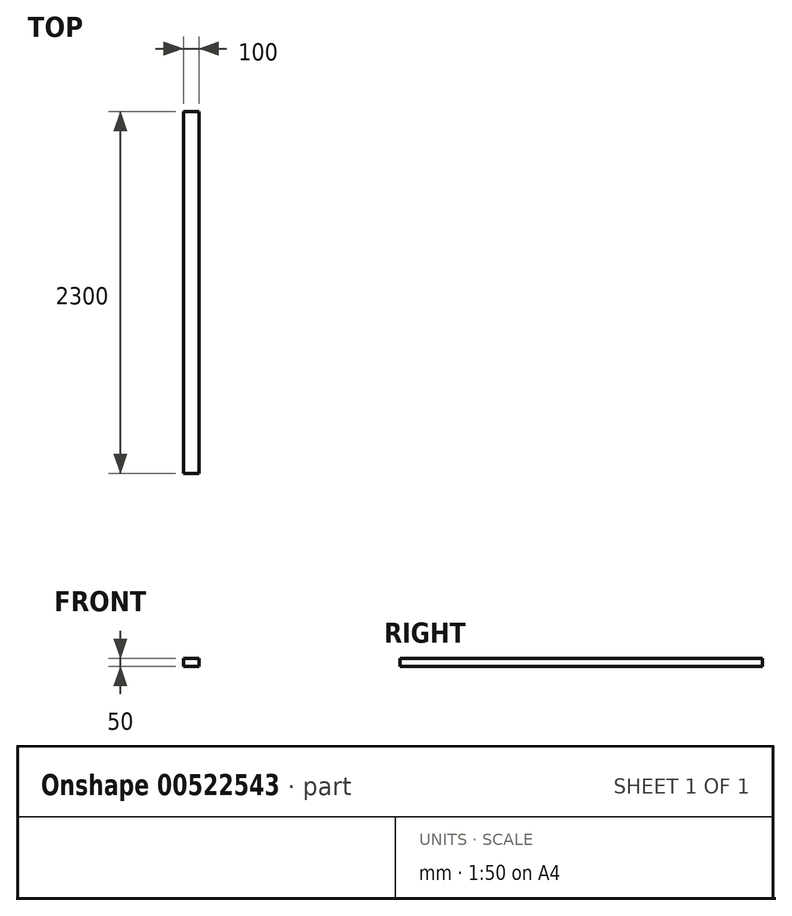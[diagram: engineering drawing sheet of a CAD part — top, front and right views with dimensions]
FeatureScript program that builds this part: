
annotation { "Feature Type Name" : "Feature", "Feature Type Description" : "" }
export const myFeature = defineFeature(function(context is Context, id is Id, definition is map)
    precondition{}
    {
        {
            var Q0;
            Q0=qCreatedBy(makeId("Front.planeOp"),FACE);
            var sketch = newSketch(context, id + "F0", { "sketchPlane" : qUnion([Q0])});
            skLineSegment(sketch, "E0.bottom", {"start": v(-139.39, 44.33) * mm, "end": v(-39.39, 44.33) * mm});
            skLineSegment(sketch, "E0.top", {"start": v(-139.39, -5.67) * mm, "end": v(-39.39, -5.67) * mm});
            skLineSegment(sketch, "E0.left", {"start": v(-139.39, 44.33) * mm, "end": v(-139.39, -5.67) * mm});
            skLineSegment(sketch, "E0.right", {"start": v(-39.39, 44.33) * mm, "end": v(-39.39, -5.67) * mm});
            skSolve(sketch);
        }
        {
            var Q0;
            Q0=qSketchRegion(id+"F0",true);
            extrude(context, id + "F1", {"entities" : qUnion([Q0]), "depth" : 2300 * mm, "offsetDistance" : 25 * mm});
        }
    });
